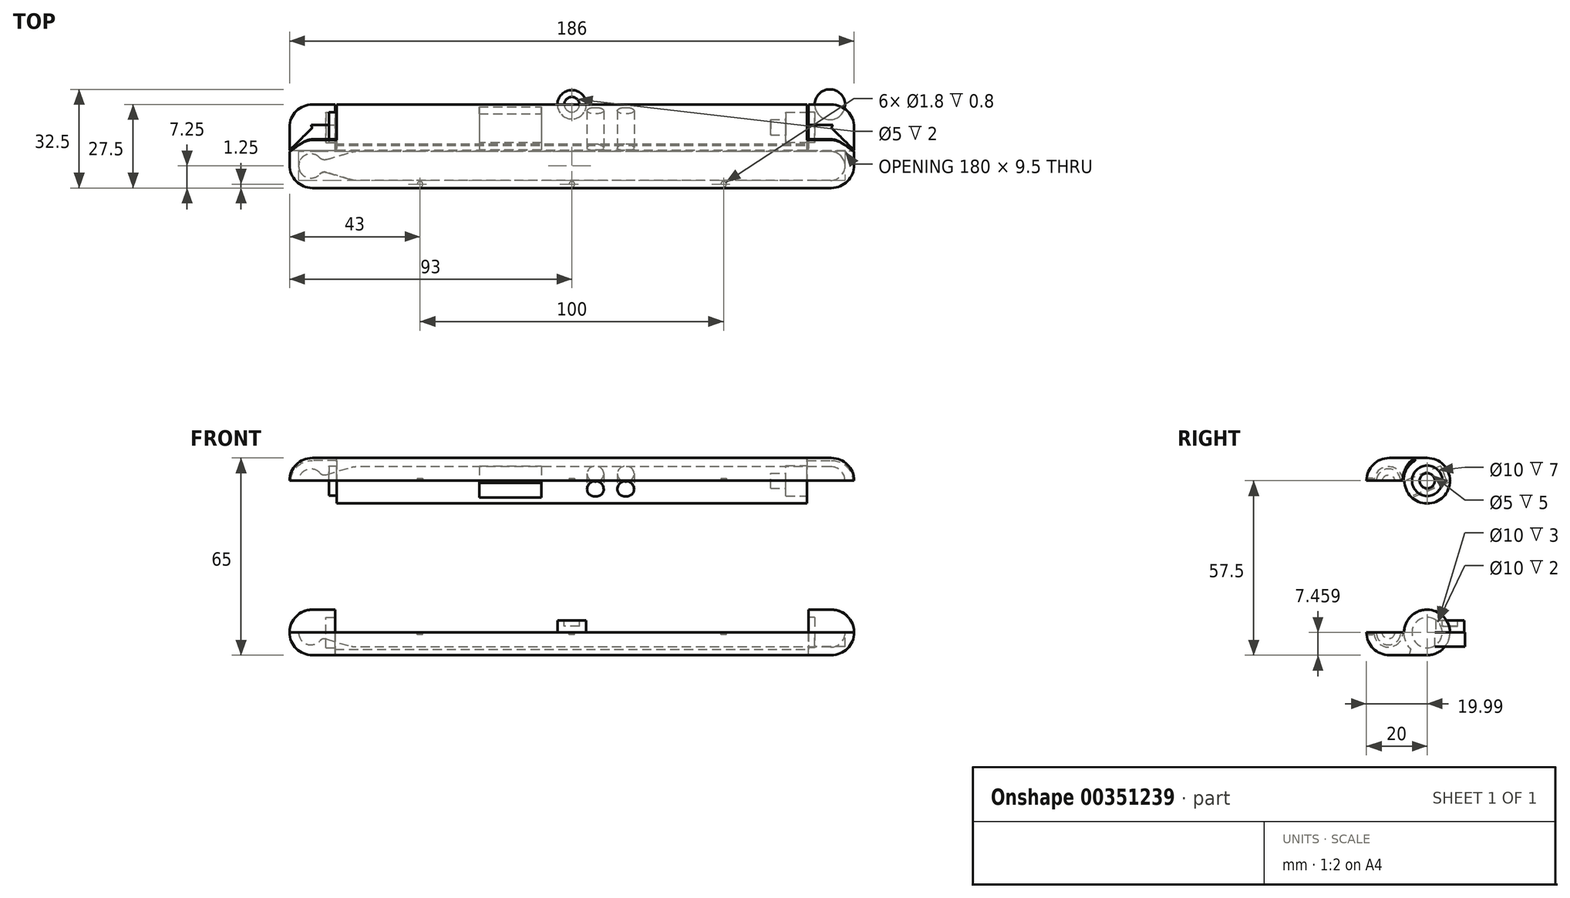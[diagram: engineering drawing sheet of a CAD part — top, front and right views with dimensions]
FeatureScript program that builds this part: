
annotation { "Feature Type Name" : "Feature", "Feature Type Description" : "" }
export const myFeature = defineFeature(function(context is Context, id is Id, definition is map)
    precondition{}
    {
        {
            var Q0;
            Q0=qCreatedBy(makeId("Front.planeOp"),FACE);
            var sketch = newSketch(context, id + "F0", { "sketchPlane" : qUnion([Q0])});
            skLineSegment(sketch, "E0.bottom", {"start": v(93, 7.5) * mm, "end": v(-93, 7.5) * mm});
            skLineSegment(sketch, "E0.top", {"start": v(93, -7.5) * mm, "end": v(-93, -7.5) * mm});
            skLineSegment(sketch, "E0.left", {"start": v(93, 7.5) * mm, "end": v(93, -7.5) * mm});
            skLineSegment(sketch, "E0.right", {"start": v(-93, 7.5) * mm, "end": v(-93, -7.5) * mm});
            skPoint(sketch, "E0.middle", {"position": v(0, 0) * mm});
            skSolve(sketch);
        }
        {
            var Q0;
            Q0=makeQuery(id+"F0.imprint","IMPRINT",FACE,{"disambiguationData":[TD([[makeQuery(id+"F0.imprint","IMPRINT",EDGE,{"derivedFrom":sQuery(id+"F0.wireOp",EDGE,"E0.bottom")}),1.0]])]});
            extrude(context, id + "F1", {"entities" : qUnion([Q0]), "depth" : 27.5 * mm});
        }
        {
            var Q0;
            Q0=makeQuery(id+"F1.opExtrude","CAP_EDGE",EDGE,{"disambiguationData":[OSD([sQuery(id+"F0.wireOp",EDGE,"E0.bottom")])],"isStart":false});
            var Q1;
            Q1=makeQuery(id+"F1.opExtrude","SWEPT_EDGE",EDGE,{"disambiguationData":[OSD([sQuery(id+"F0.wireOp",EDGE,"E0.bottom"),sQuery(id+"F0.wireOp",EDGE,"E0.left")])]});
            var Q2;
            Q2=makeQuery(id+"F1.opExtrude","CAP_EDGE",EDGE,{"disambiguationData":[OSD([sQuery(id+"F0.wireOp",EDGE,"E0.top")])],"isStart":false});
            var Q3;
            Q3=makeQuery(id+"F1.opExtrude","SWEPT_EDGE",EDGE,{"disambiguationData":[OSD([sQuery(id+"F0.wireOp",EDGE,"E0.top"),sQuery(id+"F0.wireOp",EDGE,"E0.left")])]});
            var Q4;
            Q4=makeQuery(id+"F1.opExtrude","CAP_EDGE",EDGE,{"disambiguationData":[OSD([sQuery(id+"F0.wireOp",EDGE,"E0.left")])],"isStart":false});
            var Q5;
            Q5=makeQuery(id+"F1.opExtrude","CAP_EDGE",EDGE,{"disambiguationData":[OSD([sQuery(id+"F0.wireOp",EDGE,"E0.bottom")])],"isStart":true});
            var Q6;
            Q6=makeQuery(id+"F1.opExtrude","CAP_EDGE",EDGE,{"disambiguationData":[OSD([sQuery(id+"F0.wireOp",EDGE,"E0.top")])],"isStart":true});
            var Q7;
            Q7=makeQuery(id+"F1.opExtrude","CAP_EDGE",EDGE,{"disambiguationData":[OSD([sQuery(id+"F0.wireOp",EDGE,"E0.left")])],"isStart":true});
            var Q8;
            Q8=makeQuery(id+"F1.opExtrude","CAP_EDGE",EDGE,{"disambiguationData":[OSD([sQuery(id+"F0.wireOp",EDGE,"E0.right")])],"isStart":true});
            var Q9;
            Q9=makeQuery(id+"F1.opExtrude","SWEPT_EDGE",EDGE,{"disambiguationData":[OSD([sQuery(id+"F0.wireOp",EDGE,"E0.bottom"),sQuery(id+"F0.wireOp",EDGE,"E0.right")])]});
            var Q10;
            Q10=makeQuery(id+"F1.opExtrude","SWEPT_EDGE",EDGE,{"disambiguationData":[OSD([sQuery(id+"F0.wireOp",EDGE,"E0.top"),sQuery(id+"F0.wireOp",EDGE,"E0.right")])]});
            var Q11;
            Q11=makeQuery(id+"F1.opExtrude","CAP_EDGE",EDGE,{"disambiguationData":[OSD([sQuery(id+"F0.wireOp",EDGE,"E0.right")])],"isStart":false});
            fillet(context, id + "F2", {"entities" : qUnion([Q0, Q1, Q2, Q3, Q4, Q5, Q6, Q7, Q8, Q9, Q10, Q11]), "radius" : 7.5 * mm, "tangentPropagation" : true, "allowEdgeOverflow" : false});
        }
        {
            var Q0;
            Q0=qCreatedBy(makeId("Right.planeOp"),FACE);
            cPlane(context, id + "F3", {"entities" : qUnion([Q0]), "cplaneType" : CPlaneType.OFFSET, "offset" : 78 * mm, "width" : 150 * mm, "height" : 150 * mm});
        }
        {
            var Q0;
            Q0=qCreatedBy(makeId("Front.planeOp"),FACE);
            var sketch = newSketch(context, id + "F4", { "sketchPlane" : qUnion([Q0])});
            skLineSegment(sketch, "E1", {"start": v(-72, 4.75) * mm, "end": v(85.25, 4.75) * mm});
            skLineSegment(sketch, "E2", {"start": v(-88, 0) * mm, "end": v(-72, 4.75) * mm});
            skArc(sketch, "E3", {"start": v(90, 0) * mm, "mid": v(88.6, 3.36) * mm, "end": v(85.25, 4.75) * mm});
            skLineSegment(sketch, "E4", {"start": v(-88, 0) * mm, "end": v(90, 0) * mm});
            skArc(sketch, "E5", {"start": v(-82, 0) * mm, "mid": v(-86, 4) * mm, "end": v(-90, 0) * mm});
            skLineSegment(sketch, "E6", {"start": v(-90, 0) * mm, "end": v(-82, 0) * mm});
            skSolve(sketch);
        }
        {
            var Q0;
            {var subQ0=sQuery(id+"F4.wireOp",EDGE,"E6");var subQ1=sQuery(id+"F4.wireOp",EDGE,"E2");var subQ2=makeQuery(id+"F4.imprint","INTERSECT",VERTEX,{"derivedFrom":[subQ1,subQ0]});Q0=makeQuery(id+"F4.imprint","IMPRINT",FACE,{"disambiguationData":[TD([[makeQuery(id+"F4.imprint","IMPRINT",EDGE,{"disambiguationData":[TD([[subQ2,-1.0]])],"derivedFrom":subQ1}),1.0]])]});}
            var Q1;
            {var subQ0=sQuery(id+"F4.wireOp",EDGE,"E6");var subQ1=sQuery(id+"F4.wireOp",EDGE,"E2");var subQ2=makeQuery(id+"F4.imprint","INTERSECT",VERTEX,{"derivedFrom":[subQ1,subQ0]});Q1=makeQuery(id+"F4.imprint","IMPRINT",FACE,{"disambiguationData":[TD([[makeQuery(id+"F4.imprint","IMPRINT",EDGE,{"disambiguationData":[TD([[subQ2,-1.0]])],"derivedFrom":subQ1}),-1.0]])]});}
            var Q2;
            {var subQ2=sQuery(id+"F4.wireOp",EDGE,"E1");Q2=makeQuery(id+"F4.imprint","IMPRINT",FACE,{"disambiguationData":[TD([[makeQuery(id+"F4.imprint","IMPRINT",EDGE,{"derivedFrom":subQ2}),-1.0]])]});}
            var Q3;
            Q3=sQuery(id+"F4.wireOp",EDGE,"E4");
            revolve(context, id + "F5", {"entities" : qUnion([Q0, Q1, Q2]), "axis" : qUnion([Q3]), "revolveType" : RevolveType.FULL});
        }
        {
            var Q0;
            Q0=makeQuery(id+"F5.opRevolve","SWEPT_EDGE",EDGE,{"disambiguationData":[OSD([sQuery(id+"F4.wireOp",EDGE,"E2"),sQuery(id+"F4.wireOp",EDGE,"E5")])]});
            fillet(context, id + "F6", {"entities" : qUnion([Q0]), "radius" : 2 * mm, "tangentPropagation" : true, "allowEdgeOverflow" : false});
        }
        {
            var Q0;
            Q0=makeQuery(id+"F5.opRevolve","SWEPT_EDGE",EDGE,{"disambiguationData":[OSD([sQuery(id+"F4.wireOp",EDGE,"E1"),sQuery(id+"F4.wireOp",EDGE,"E2")])]});
            fillet(context, id + "F7", {"entities" : qUnion([Q0]), "radius" : 5 * mm, "tangentPropagation" : true, "allowEdgeOverflow" : false});
        }
        {
            var Q0;
            Q0=qCreatedBy(makeId("Top.planeOp"),FACE);
            var sketch = newSketch(context, id + "F8", { "sketchPlane" : qUnion([Q0])});
            skCircle(sketch, "E7", {"center": v(85, 0) * mm, "radius": 5 * mm});
            skSolve(sketch);
        }
        {
            var Q0;
            Q0=makeQuery(id+"F8.imprint","IMPRINT",FACE,{"disambiguationData":[TD([[makeQuery(id+"F8.imprint","IMPRINT",EDGE,{"derivedFrom":sQuery(id+"F8.wireOp",EDGE,"E7")}),1.0]])]});
            extrude(context, id + "F9", {"entities" : qUnion([Q0]), "oppositeDirection" : true, "depth" : 4.75 * mm});
        }
        {
            var Q0;
            Q0=makeQuery(id+"F5.opRevolve","SWEPT_BODY",BODY,{"disambiguationData":[OSD([sQuery(id+"F4.wireOp",EDGE,"E1"),sQuery(id+"F4.wireOp",EDGE,"E2"),sQuery(id+"F4.wireOp",EDGE,"E3"),sQuery(id+"F4.wireOp",EDGE,"E4"),sQuery(id+"F4.wireOp",EDGE,"E5"),sQuery(id+"F4.wireOp",EDGE,"E6")])]});
            transform(context, id + "F10", {"entities" : qUnion([Q0]), "transformType" : TransformType.TRANSLATION_3D, "dx" : 0 * mm, "dy" : -20.25 * mm, "dz" : -0.1 * mm, "makeCopy" : false});
        }
        {
            var Q0;
            Q0=makeQuery(id+"F5.opRevolve","SWEPT_BODY",BODY,{"disambiguationData":[OSD([sQuery(id+"F4.wireOp",EDGE,"E1"),sQuery(id+"F4.wireOp",EDGE,"E2"),sQuery(id+"F4.wireOp",EDGE,"E3"),sQuery(id+"F4.wireOp",EDGE,"E4"),sQuery(id+"F4.wireOp",EDGE,"E5"),sQuery(id+"F4.wireOp",EDGE,"E6")])]});
            var Q1;
            Q1=makeQuery(id+"F1.opExtrude","SWEPT_BODY",BODY,{"disambiguationData":[OSD([sQuery(id+"F0.wireOp",EDGE,"E0.bottom"),sQuery(id+"F0.wireOp",EDGE,"E0.top"),sQuery(id+"F0.wireOp",EDGE,"E0.left"),sQuery(id+"F0.wireOp",EDGE,"E0.right")])]});
            booleanBodies(context, id + "F11", {"operationType" : BooleanOperationType.SUBTRACTION, "tools" : qUnion([Q0]), "targets" : qUnion([Q1]), "keepTools" : true});
        }
        {
            var Q0;
            Q0=makeQuery(id+"F1.opExtrude","SWEPT_BODY",BODY,{"disambiguationData":[OSD([sQuery(id+"F0.wireOp",EDGE,"E0.bottom"),sQuery(id+"F0.wireOp",EDGE,"E0.top"),sQuery(id+"F0.wireOp",EDGE,"E0.left"),sQuery(id+"F0.wireOp",EDGE,"E0.right")])]});
            transform(context, id + "F12", {"entities" : qUnion([Q0]), "transformType" : TransformType.TRANSLATION_3D, "dx" : 0 * mm, "dy" : 0 * mm, "dz" : 50 * mm, "makeCopy" : true});
        }
        {
            var Q0;
            Q0=qCreatedBy(makeId("Right.planeOp"),FACE);
            cPlane(context, id + "F13", {"entities" : qUnion([Q0]), "cplaneType" : CPlaneType.OFFSET, "offset" : 93 * mm, "width" : 150 * mm, "height" : 150 * mm});
        }
        {
            var Q0;
            Q0=qCreatedBy(makeId("Right.planeOp"),FACE);
            cPlane(context, id + "F14", {"entities" : qUnion([Q0]), "cplaneType" : CPlaneType.OFFSET, "offset" : 93 * mm, "oppositeDirection" : true, "width" : 150 * mm, "height" : 150 * mm});
        }
        {
            var Q0;
            Q0=qCreatedBy(id+"F13.planeOp",FACE);
            var sketch = newSketch(context, id + "F15", { "sketchPlane" : qUnion([Q0])});
            skCircle(sketch, "E8", {"center": v(-7.6, 0) * mm, "radius": 7.5 * mm});
            skLineSegment(sketch, "E9.bottom", {"start": v(-6.72, 0) * mm, "end": v(-52.07, 0) * mm});
            skLineSegment(sketch, "E9.top", {"start": v(-6.72, 20.65) * mm, "end": v(-52.07, 20.65) * mm});
            skLineSegment(sketch, "E9.left", {"start": v(-6.72, 0) * mm, "end": v(-6.72, 20.65) * mm});
            skLineSegment(sketch, "E9.right", {"start": v(-52.07, 0) * mm, "end": v(-52.07, 20.65) * mm});
            skPoint(sketch, "E9.middle", {"position": v(-29.4, 10.33) * mm});
            skSolve(sketch);
        }
        {
            var Q0;
            {var subQ1=sQuery(id+"F15.wireOp",EDGE,"E9.top");Q0=makeQuery(id+"F15.imprint","IMPRINT",FACE,{"disambiguationData":[TD([[makeQuery(id+"F15.imprint","IMPRINT",EDGE,{"derivedFrom":subQ1}),1.0]])]});}
            extrude(context, id + "F16", {"entities" : qUnion([Q0]), "operationType" : NewBodyOperationType.REMOVE, "endBound" : BoundingType.THROUGH_ALL, "oppositeDirection" : true, "depth" : 25 * mm});
        }
        {
            var Q0;
            Q0=qCreatedBy(id+"F13.planeOp",FACE);
            var sketch = newSketch(context, id + "F17", { "sketchPlane" : qUnion([Q0])});
            skCircle(sketch, "E10", {"center": v(-7.5, 50) * mm, "radius": 7.5 * mm});
            skLineSegment(sketch, "E11.bottom", {"start": v(-7.5, 50) * mm, "end": v(-34.83, 50) * mm});
            skLineSegment(sketch, "E11.top", {"start": v(-7.5, 41.08) * mm, "end": v(-34.83, 41.08) * mm});
            skLineSegment(sketch, "E11.left", {"start": v(-7.5, 50) * mm, "end": v(-7.5, 41.08) * mm});
            skLineSegment(sketch, "E11.right", {"start": v(-34.83, 50) * mm, "end": v(-34.83, 41.08) * mm});
            skSolve(sketch);
        }
        {
            var Q0;
            {var subQ1=sQuery(id+"F17.wireOp",EDGE,"E11.top");Q0=makeQuery(id+"F17.imprint","IMPRINT",FACE,{"disambiguationData":[TD([[makeQuery(id+"F17.imprint","IMPRINT",EDGE,{"derivedFrom":subQ1}),-1.0]])]});}
            extrude(context, id + "F18", {"entities" : qUnion([Q0]), "operationType" : NewBodyOperationType.REMOVE, "endBound" : BoundingType.THROUGH_ALL, "oppositeDirection" : true, "depth" : 25 * mm});
        }
        {
            var Q0;
            Q0=qCreatedBy(id+"F13.planeOp",FACE);
            var sketch = newSketch(context, id + "F19", { "sketchPlane" : qUnion([Q0])});
            skCircle(sketch, "E12", {"center": v(-7.5, 50) * mm, "radius": 7.8 * mm});
            skSolve(sketch);
        }
        {
            var Q0;
            Q0=makeQuery(id+"F19.imprint","IMPRINT",FACE,{"disambiguationData":[TD([[makeQuery(id+"F19.imprint","IMPRINT",EDGE,{"derivedFrom":sQuery(id+"F19.wireOp",EDGE,"E12")}),1.0]])]});
            extrude(context, id + "F20", {"entities" : qUnion([Q0]), "operationType" : NewBodyOperationType.REMOVE, "oppositeDirection" : true, "depth" : 15.5 * mm});
        }
        {
            var Q0;
            Q0=qCreatedBy(id+"F14.planeOp",FACE);
            var sketch = newSketch(context, id + "F21", { "sketchPlane" : qUnion([Q0])});
            skCircle(sketch, "E13", {"center": v(-7.5, 50) * mm, "radius": 7.8 * mm});
            skSolve(sketch);
        }
        {
            var Q0;
            Q0=makeQuery(id+"F21.imprint","IMPRINT",FACE,{"disambiguationData":[TD([[makeQuery(id+"F21.imprint","IMPRINT",EDGE,{"derivedFrom":sQuery(id+"F21.wireOp",EDGE,"E13")}),1.0]])]});
            extrude(context, id + "F22", {"entities" : qUnion([Q0]), "operationType" : NewBodyOperationType.REMOVE, "depth" : 15.5 * mm});
        }
        {
            var Q0;
            Q0=qCreatedBy(id+"F3.planeOp",FACE);
            var sketch = newSketch(context, id + "F23", { "sketchPlane" : qUnion([Q0])});
            skCircle(sketch, "E14", {"center": v(-7.5, 0) * mm, "radius": 7.75 * mm});
            skSolve(sketch);
        }
        {
            var Q0;
            Q0=makeQuery(id+"F23.imprint","IMPRINT",FACE,{"disambiguationData":[TD([[makeQuery(id+"F23.imprint","IMPRINT",EDGE,{"derivedFrom":sQuery(id+"F23.wireOp",EDGE,"E14")}),1.0]])]});
            extrude(context, id + "F24", {"entities" : qUnion([Q0]), "oppositeDirection" : true, "depth" : 156 * mm});
        }
        {
            var Q0;
            Q0=makeQuery(id+"F24.opExtrude","SWEPT_BODY",BODY,{"disambiguationData":[OSD([sQuery(id+"F23.wireOp",EDGE,"E14")])]});
            var Q1;
            Q1=makeQuery(id+"F1.opExtrude","SWEPT_BODY",BODY,{"disambiguationData":[OSD([sQuery(id+"F0.wireOp",EDGE,"E0.bottom"),sQuery(id+"F0.wireOp",EDGE,"E0.top"),sQuery(id+"F0.wireOp",EDGE,"E0.left"),sQuery(id+"F0.wireOp",EDGE,"E0.right")])]});
            booleanBodies(context, id + "F25", {"operationType" : BooleanOperationType.SUBTRACTION, "tools" : qUnion([Q0]), "targets" : qUnion([Q1])});
        }
        {
            var Q0;
            Q0=qCreatedBy(makeId("Front.planeOp"),FACE);
            cPlane(context, id + "F26", {"entities" : qUnion([Q0]), "cplaneType" : CPlaneType.OFFSET, "offset" : 16 * mm, "width" : 150 * mm, "height" : 150 * mm});
        }
        {
            var Q0;
            Q0=qCreatedBy(id+"F26.planeOp",FACE);
            var sketch = newSketch(context, id + "F27", { "sketchPlane" : qUnion([Q0])});
            skLineSegment(sketch, "E15.bottom", {"start": v(-30.5, 50) * mm, "end": v(-10, 50) * mm});
            skLineSegment(sketch, "E15.top", {"start": v(-30.5, 44) * mm, "end": v(-10, 44) * mm});
            skLineSegment(sketch, "E15.left", {"start": v(-30.5, 50) * mm, "end": v(-30.5, 44) * mm});
            skLineSegment(sketch, "E15.right", {"start": v(-10, 50) * mm, "end": v(-10, 44) * mm});
            skCircle(sketch, "E16", {"center": v(7.75, 47.25) * mm, "radius": 2.75 * mm});
            skCircle(sketch, "E17", {"center": v(17.75, 47.25) * mm, "radius": 2.75 * mm});
            skSolve(sketch);
        }
        {
            var Q0;
            Q0=makeQuery(id+"F27.imprint","IMPRINT",FACE,{"disambiguationData":[TD([[makeQuery(id+"F27.imprint","IMPRINT",EDGE,{"derivedFrom":sQuery(id+"F27.wireOp",EDGE,"E15.bottom")}),-1.0]])]});
            var Q1;
            Q1=makeQuery(id+"F27.imprint","IMPRINT",FACE,{"disambiguationData":[TD([[makeQuery(id+"F27.imprint","IMPRINT",EDGE,{"derivedFrom":sQuery(id+"F27.wireOp",EDGE,"E16")}),1.0]])]});
            var Q2;
            Q2=makeQuery(id+"F27.imprint","IMPRINT",FACE,{"disambiguationData":[TD([[makeQuery(id+"F27.imprint","IMPRINT",EDGE,{"derivedFrom":sQuery(id+"F27.wireOp",EDGE,"E17")}),1.0]])]});
            extrude(context, id + "F28", {"entities" : qUnion([Q0, Q1, Q2]), "oppositeDirection" : true, "depth" : 14 * mm});
        }
        {
            var Q0;
            Q0=makeQuery(id+"F28.opExtrude","SWEPT_BODY",BODY,{"disambiguationData":[OSD([sQuery(id+"F27.wireOp",EDGE,"E15.bottom"),sQuery(id+"F27.wireOp",EDGE,"E15.top"),sQuery(id+"F27.wireOp",EDGE,"E15.left"),sQuery(id+"F27.wireOp",EDGE,"E15.right")])]});
            var Q1;
            Q1=makeQuery(id+"F28.opExtrude","SWEPT_BODY",BODY,{"disambiguationData":[OSD([sQuery(id+"F27.wireOp",EDGE,"E16")])]});
            var Q2;
            Q2=makeQuery(id+"F28.opExtrude","SWEPT_BODY",BODY,{"disambiguationData":[OSD([sQuery(id+"F27.wireOp",EDGE,"E17")])]});
            var Q3;
            Q3=makeQuery(id+"F28.opExtrude","CAP_EDGE",EDGE,{"disambiguationData":[OSD([sQuery(id+"F27.wireOp",EDGE,"E15.bottom")])],"isStart":true});
            transform(context, id + "F29", {"entities" : qUnion([Q0, Q1, Q2]), "transformType" : TransformType.ROTATION, "transformAxis" : qUnion([Q3]), "angle" : 22.33 * degree, "makeCopy" : false});
        }
        {
            var Q0;
            Q0=makeQuery(id+"F28.opExtrude","SWEPT_BODY",BODY,{"disambiguationData":[OSD([sQuery(id+"F27.wireOp",EDGE,"E15.bottom"),sQuery(id+"F27.wireOp",EDGE,"E15.top"),sQuery(id+"F27.wireOp",EDGE,"E15.left"),sQuery(id+"F27.wireOp",EDGE,"E15.right")])]});
            transform(context, id + "F30", {"entities" : qUnion([Q0]), "transformType" : TransformType.TRANSLATION_3D, "dx" : 0 * mm, "dy" : 0 * mm, "dz" : -0.5 * mm, "makeCopy" : false});
        }
        {
            var Q0;
            Q0=makeQuery(id+"F28.opExtrude","SWEPT_BODY",BODY,{"disambiguationData":[OSD([sQuery(id+"F27.wireOp",EDGE,"E16")])]});
            transform(context, id + "F31", {"entities" : qUnion([Q0]), "transformType" : TransformType.TRANSLATION_3D, "dx" : 0 * mm, "dy" : 0 * mm, "dz" : -0.5 * mm, "makeCopy" : false});
        }
        {
            var Q0;
            Q0=makeQuery(id+"F28.opExtrude","SWEPT_BODY",BODY,{"disambiguationData":[OSD([sQuery(id+"F27.wireOp",EDGE,"E17")])]});
            transform(context, id + "F32", {"entities" : qUnion([Q0]), "transformType" : TransformType.TRANSLATION_3D, "dx" : 0 * mm, "dy" : 0 * mm, "dz" : -0.5 * mm, "makeCopy" : false});
        }
        {
            var Q0;
            Q0=makeQuery(id+"F28.opExtrude","SWEPT_BODY",BODY,{"disambiguationData":[OSD([sQuery(id+"F27.wireOp",EDGE,"E15.bottom"),sQuery(id+"F27.wireOp",EDGE,"E15.top"),sQuery(id+"F27.wireOp",EDGE,"E15.left"),sQuery(id+"F27.wireOp",EDGE,"E15.right")])]});
            var Q1;
            Q1=makeQuery(id+"F28.opExtrude","SWEPT_BODY",BODY,{"disambiguationData":[OSD([sQuery(id+"F27.wireOp",EDGE,"E16")])]});
            var Q2;
            Q2=makeQuery(id+"F28.opExtrude","SWEPT_BODY",BODY,{"disambiguationData":[OSD([sQuery(id+"F27.wireOp",EDGE,"E17")])]});
            var Q3;
            Q3=makeQuery(id+"F12.opPattern","COPY",BODY,{"derivedFrom":makeQuery(id+"F1.opExtrude","SWEPT_BODY",BODY,{"disambiguationData":[OSD([sQuery(id+"F0.wireOp",EDGE,"E0.bottom"),sQuery(id+"F0.wireOp",EDGE,"E0.top"),sQuery(id+"F0.wireOp",EDGE,"E0.left"),sQuery(id+"F0.wireOp",EDGE,"E0.right")])]}),"instanceName":"1"});
            booleanBodies(context, id + "F33", {"operationType" : BooleanOperationType.SUBTRACTION, "tools" : qUnion([Q0, Q1, Q2]), "targets" : qUnion([Q3])});
        }
        {
            var Q0;
            Q0=makeQuery(id+"F25.opBoolean","COPY",FACE,{"derivedFrom":makeQuery(id+"F24.opExtrude","CAP_FACE",FACE,{"disambiguationData":[OSD([sQuery(id+"F23.wireOp",EDGE,"E14")])],"isStart":false})});
            var sketch = newSketch(context, id + "F34", { "sketchPlane" : qUnion([Q0])});
            skCircle(sketch, "E18", {"center": v(-7.51, -0.04) * mm, "radius": 5 * mm});
            skSolve(sketch);
        }
        {
            var Q0;
            Q0=makeQuery(id+"F34.imprint","IMPRINT",FACE,{"disambiguationData":[TD([[makeQuery(id+"F34.imprint","IMPRINT",EDGE,{"derivedFrom":sQuery(id+"F34.wireOp",EDGE,"E18")}),1.0]])]});
            extrude(context, id + "F35", {"entities" : qUnion([Q0]), "operationType" : NewBodyOperationType.REMOVE, "oppositeDirection" : true, "depth" : 3 * mm});
        }
        {
            var Q0;
            Q0=makeQuery(id+"F20.boolean.opBoolean","COPY",FACE,{"derivedFrom":makeQuery(id+"F20.opExtrude","CAP_FACE",FACE,{"disambiguationData":[OSD([sQuery(id+"F19.wireOp",EDGE,"E12")])],"isStart":false})});
            var sketch = newSketch(context, id + "F36", { "sketchPlane" : qUnion([Q0])});
            skCircle(sketch, "E19", {"center": v(-7.5, 50) * mm, "radius": 5 * mm});
            skSolve(sketch);
        }
        {
            var Q0;
            Q0=makeQuery(id+"F36.imprint","IMPRINT",FACE,{"disambiguationData":[TD([[makeQuery(id+"F36.imprint","IMPRINT",EDGE,{"derivedFrom":sQuery(id+"F36.wireOp",EDGE,"E19")}),1.0]])]});
            extrude(context, id + "F37", {"entities" : qUnion([Q0]), "operationType" : NewBodyOperationType.REMOVE, "oppositeDirection" : true, "depth" : 7 * mm});
        }
        {
            var Q0;
            Q0=makeQuery(id+"F22.boolean.opBoolean","COPY",FACE,{"derivedFrom":makeQuery(id+"F22.opExtrude","CAP_FACE",FACE,{"disambiguationData":[OSD([sQuery(id+"F21.wireOp",EDGE,"E13")])],"isStart":false})});
            var sketch = newSketch(context, id + "F38", { "sketchPlane" : qUnion([Q0])});
            skCircle(sketch, "E20", {"center": v(7.5, 50) * mm, "radius": 4.9 * mm});
            skSolve(sketch);
        }
        {
            var Q0;
            Q0=makeQuery(id+"F38.imprint","IMPRINT",FACE,{"disambiguationData":[TD([[makeQuery(id+"F38.imprint","IMPRINT",EDGE,{"derivedFrom":sQuery(id+"F38.wireOp",EDGE,"E20")}),1.0]])]});
            extrude(context, id + "F39", {"entities" : qUnion([Q0]), "operationType" : NewBodyOperationType.ADD, "depth" : 2.5 * mm});
        }
        {
            var Q0;
            Q0=makeQuery(id+"F25.opBoolean","COPY",FACE,{"derivedFrom":makeQuery(id+"F24.opExtrude","CAP_FACE",FACE,{"disambiguationData":[OSD([sQuery(id+"F23.wireOp",EDGE,"E14")])],"isStart":true})});
            var sketch = newSketch(context, id + "F40", { "sketchPlane" : qUnion([Q0])});
            skCircle(sketch, "E21", {"center": v(7.51, -0.04) * mm, "radius": 5 * mm});
            skSolve(sketch);
        }
        {
            var Q0;
            Q0=makeQuery(id+"F40.imprint","IMPRINT",FACE,{"disambiguationData":[TD([[makeQuery(id+"F40.imprint","IMPRINT",EDGE,{"derivedFrom":sQuery(id+"F40.wireOp",EDGE,"E21")}),1.0]])]});
            extrude(context, id + "F41", {"entities" : qUnion([Q0]), "operationType" : NewBodyOperationType.REMOVE, "oppositeDirection" : true, "depth" : 2 * mm});
        }
        {
            var Q0;
            Q0=makeQuery(id+"F16.boolean.opBoolean","COPY",FACE,{"derivedFrom":makeQuery(id+"F16.opExtrude","SWEPT_FACE",FACE,{"disambiguationData":[OSD([sQuery(id+"F15.wireOp",EDGE,"E9.bottom")])]})});
            var sketch = newSketch(context, id + "F42", { "sketchPlane" : qUnion([Q0])});
            skCircle(sketch, "E22", {"center": v(0, -26.25) * mm, "radius": 0.9 * mm});
            skCircle(sketch, "E23", {"center": v(-50, -26.25) * mm, "radius": 0.9 * mm});
            skCircle(sketch, "E24", {"center": v(50, -26.25) * mm, "radius": 0.9 * mm});
            skSolve(sketch);
        }
        {
            var Q0;
            Q0=makeQuery(id+"F42.imprint","IMPRINT",FACE,{"disambiguationData":[TD([[makeQuery(id+"F42.imprint","IMPRINT",EDGE,{"derivedFrom":sQuery(id+"F42.wireOp",EDGE,"E24")}),1.0]])]});
            var Q1;
            Q1=makeQuery(id+"F42.imprint","IMPRINT",FACE,{"disambiguationData":[TD([[makeQuery(id+"F42.imprint","IMPRINT",EDGE,{"derivedFrom":sQuery(id+"F42.wireOp",EDGE,"E22")}),1.0]])]});
            var Q2;
            Q2=makeQuery(id+"F42.imprint","IMPRINT",FACE,{"disambiguationData":[TD([[makeQuery(id+"F42.imprint","IMPRINT",EDGE,{"derivedFrom":sQuery(id+"F42.wireOp",EDGE,"E23")}),1.0]])]});
            extrude(context, id + "F43", {"entities" : qUnion([Q0, Q1, Q2]), "operationType" : NewBodyOperationType.REMOVE, "oppositeDirection" : true, "depth" : 0.8 * mm});
        }
        {
            var Q0;
            Q0=makeQuery(id+"F18.boolean.opBoolean","COPY",FACE,{"derivedFrom":makeQuery(id+"F18.opExtrude","SWEPT_FACE",FACE,{"disambiguationData":[OSD([sQuery(id+"F17.wireOp",EDGE,"E11.bottom")])]})});
            var sketch = newSketch(context, id + "F44", { "sketchPlane" : qUnion([Q0])});
            skCircle(sketch, "E25", {"center": v(-50, 26.25) * mm, "radius": 0.9 * mm});
            skCircle(sketch, "E26", {"center": v(0, 26.25) * mm, "radius": 0.9 * mm});
            skCircle(sketch, "E27", {"center": v(50, 26.25) * mm, "radius": 0.9 * mm});
            skSolve(sketch);
        }
        {
            var Q0;
            Q0=makeQuery(id+"F44.imprint","IMPRINT",FACE,{"disambiguationData":[TD([[makeQuery(id+"F44.imprint","IMPRINT",EDGE,{"derivedFrom":sQuery(id+"F44.wireOp",EDGE,"E25")}),1.0]])]});
            var Q1;
            Q1=makeQuery(id+"F44.imprint","IMPRINT",FACE,{"disambiguationData":[TD([[makeQuery(id+"F44.imprint","IMPRINT",EDGE,{"derivedFrom":sQuery(id+"F44.wireOp",EDGE,"E26")}),1.0]])]});
            var Q2;
            Q2=makeQuery(id+"F44.imprint","IMPRINT",FACE,{"disambiguationData":[TD([[makeQuery(id+"F44.imprint","IMPRINT",EDGE,{"derivedFrom":sQuery(id+"F44.wireOp",EDGE,"E27")}),1.0]])]});
            extrude(context, id + "F45", {"entities" : qUnion([Q0, Q1, Q2]), "operationType" : NewBodyOperationType.REMOVE, "oppositeDirection" : true, "depth" : 0.8 * mm});
        }
        {
            var Q0;
            Q0=makeQuery(id+"F37.boolean.opBoolean","COPY",FACE,{"derivedFrom":makeQuery(id+"F37.opExtrude","CAP_FACE",FACE,{"disambiguationData":[OSD([sQuery(id+"F36.wireOp",EDGE,"E19")])],"isStart":false})});
            var sketch = newSketch(context, id + "F46", { "sketchPlane" : qUnion([Q0])});
            skCircle(sketch, "E28", {"center": v(-7.5, 50) * mm, "radius": 2.5 * mm});
            skSolve(sketch);
        }
        {
            var Q0;
            Q0=makeQuery(id+"F46.imprint","IMPRINT",FACE,{"disambiguationData":[TD([[makeQuery(id+"F46.imprint","IMPRINT",EDGE,{"derivedFrom":sQuery(id+"F46.wireOp",EDGE,"E28")}),1.0]])]});
            extrude(context, id + "F47", {"entities" : qUnion([Q0]), "operationType" : NewBodyOperationType.REMOVE, "oppositeDirection" : true, "depth" : 5 * mm});
        }
        {
            var Q0;
            Q0=qCreatedBy(makeId("Top.planeOp"),FACE);
            var sketch = newSketch(context, id + "F48", { "sketchPlane" : qUnion([Q0])});
            skCircle(sketch, "E29", {"center": v(0, 0) * mm, "radius": 4.75 * mm});
            skSolve(sketch);
        }
        {
            var Q0;
            Q0=makeQuery(id+"F48.imprint","IMPRINT",FACE,{"disambiguationData":[TD([[makeQuery(id+"F48.imprint","IMPRINT",EDGE,{"derivedFrom":sQuery(id+"F48.wireOp",EDGE,"E29")}),1.0]])]});
            extrude(context, id + "F49", {"entities" : qUnion([Q0]), "depth" : 4 * mm});
        }
        {
            var Q0;
            Q0=makeQuery(id+"F49.opExtrude","CAP_FACE",FACE,{"disambiguationData":[OSD([sQuery(id+"F48.wireOp",EDGE,"E29")])],"isStart":false});
            var sketch = newSketch(context, id + "F50", { "sketchPlane" : qUnion([Q0])});
            skCircle(sketch, "E30", {"center": v(0, 0) * mm, "radius": 2.5 * mm});
            skSolve(sketch);
        }
        {
            var Q0;
            Q0=makeQuery(id+"F50.imprint","IMPRINT",FACE,{"disambiguationData":[TD([[makeQuery(id+"F50.imprint","IMPRINT",EDGE,{"derivedFrom":sQuery(id+"F50.wireOp",EDGE,"E30")}),1.0]])]});
            extrude(context, id + "F51", {"entities" : qUnion([Q0]), "operationType" : NewBodyOperationType.REMOVE, "oppositeDirection" : true, "depth" : 2 * mm});
        }
        {
            var Q0;
            Q0=makeQuery(id+"F25.opBoolean","INTERSECT",EDGE,{"derivedFrom":[makeQuery(id+"F1.opExtrude","SWEPT_FACE",FACE,{"disambiguationData":[OSD([sQuery(id+"F0.wireOp",EDGE,"E0.top")])]}),makeQuery(id+"F24.opExtrude","SWEPT_FACE",FACE,{"disambiguationData":[OSD([sQuery(id+"F23.wireOp",EDGE,"E14")])]})]});
            chamfer(context, id + "F52", {"entities" : qUnion([Q0]), "width" : 4 * mm, "tangentPropagation" : true});
        }
        {
            var Q0;
            Q0=makeQuery(id+"F20.boolean.opBoolean","INTERSECT",EDGE,{"derivedFrom":[makeQuery(id+"F12.opPattern","COPY",FACE,{"derivedFrom":makeQuery(id+"F1.opExtrude","SWEPT_FACE",FACE,{"disambiguationData":[OSD([sQuery(id+"F0.wireOp",EDGE,"E0.bottom")])]}),"instanceName":"1"}),makeQuery(id+"F20.opExtrude","SWEPT_FACE",FACE,{"disambiguationData":[OSD([sQuery(id+"F19.wireOp",EDGE,"E12")])]})]});
            var Q1;
            Q1=makeQuery(id+"F22.boolean.opBoolean","INTERSECT",EDGE,{"derivedFrom":[makeQuery(id+"F12.opPattern","COPY",FACE,{"derivedFrom":makeQuery(id+"F1.opExtrude","SWEPT_FACE",FACE,{"disambiguationData":[OSD([sQuery(id+"F0.wireOp",EDGE,"E0.bottom")])]}),"instanceName":"1"}),makeQuery(id+"F22.opExtrude","SWEPT_FACE",FACE,{"disambiguationData":[OSD([sQuery(id+"F21.wireOp",EDGE,"E13")])]})]});
            chamfer(context, id + "F53", {"entities" : qUnion([Q0, Q1]), "width" : 2 * mm, "tangentPropagation" : true});
        }
    });
